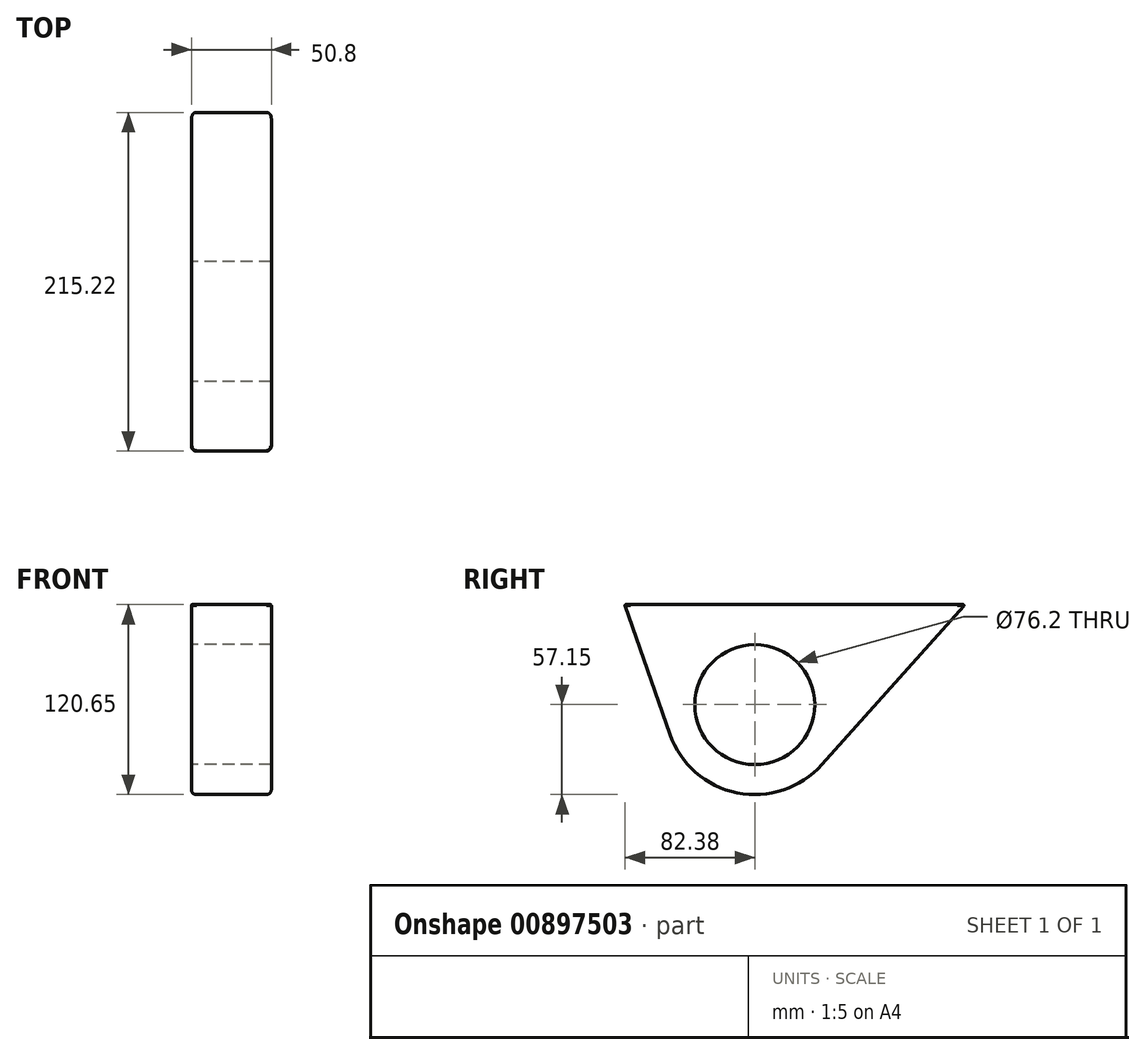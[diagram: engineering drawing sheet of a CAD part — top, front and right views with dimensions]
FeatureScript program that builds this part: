
annotation { "Feature Type Name" : "Feature", "Feature Type Description" : "" }
export const myFeature = defineFeature(function(context is Context, id is Id, definition is map)
    precondition{}
    {
        {
            var Q0;
            Q0=qCreatedBy(makeId("Right.planeOp"),FACE);
            var sketch = newSketch(context, id + "F0", { "sketchPlane" : qUnion([Q0])});
            skCircle(sketch, "E0", {"center": v(0, 0) * mm, "radius": 38.1 * mm});
            skCircle(sketch, "E1.0", {"center": v(0, 0) * mm, "radius": 57.15 * mm});
            skLineSegment(sketch, "E2", {"start": v(-82.55, 63.5) * mm, "end": v(133.35, 63.5) * mm});
            skLineSegment(sketch, "E3", {"start": v(0, 0) * mm, "end": v(0, 63.5) * mm, "construction": true});
            skLineSegment(sketch, "E4", {"start": v(-82.55, 63.5) * mm, "end": v(-53.99, -18.75) * mm});
            skLineSegment(sketch, "E5", {"start": v(133.35, 63.5) * mm, "end": v(42.62, -38.07) * mm});
            skSolve(sketch);
        }
        {
            var Q0;
            Q0=makeQuery(id+"F0.imprint","IMPRINT",FACE,{"disambiguationData":[TD([[makeQuery(id+"F0.imprint","IMPRINT",EDGE,{"derivedFrom":sQuery(id+"F0.wireOp",EDGE,"E0")}),-1.0]])]});
            var Q1;
            Q1=makeQuery(id+"F0.imprint","IMPRINT",FACE,{"disambiguationData":[TD([[makeQuery(id+"F0.imprint","IMPRINT",EDGE,{"derivedFrom":sQuery(id+"F0.wireOp",EDGE,"E2")}),-1.0]])]});
            extrude(context, id + "F1", {"entities" : qUnion([Q0, Q1]), "depth" : 50.8 * mm, "offsetDistance" : 25.4 * mm});
        }
        {
            var Q0;
            Q0=makeQuery(id+"F1.opExtrude","CAP_EDGE",EDGE,{"disambiguationData":[OSD([sQuery(id+"F0.wireOp",EDGE,"E0")])],"isStart":true});
            var Q1;
            Q1=makeQuery(id+"F1.opExtrude","CAP_EDGE",EDGE,{"disambiguationData":[OSD([sQuery(id+"F0.wireOp",EDGE,"E0")])],"isStart":false});
            var Q2;
            Q2=makeQuery(id+"F1.opExtrude","CAP_EDGE",EDGE,{"disambiguationData":[OSD([sQuery(id+"F0.wireOp",EDGE,"E2")])],"isStart":false});
            var Q3;
            Q3=makeQuery(id+"F1.opExtrude","SWEPT_EDGE",EDGE,{"disambiguationData":[OSD([sQuery(id+"F0.wireOp",EDGE,"E2"),sQuery(id+"F0.wireOp",EDGE,"E5")])]});
            var Q4;
            Q4=makeQuery(id+"F1.opExtrude","CAP_EDGE",EDGE,{"disambiguationData":[OSD([sQuery(id+"F0.wireOp",EDGE,"E2")])],"isStart":true});
            var Q5;
            Q5=makeQuery(id+"F1.opExtrude","SWEPT_EDGE",EDGE,{"disambiguationData":[OSD([sQuery(id+"F0.wireOp",EDGE,"E2"),sQuery(id+"F0.wireOp",EDGE,"E4")])]});
            fillet(context, id + "F2", {"entities" : qUnion([Q0, Q1, Q2, Q3, Q4, Q5]), "radius" : 0.4 * mm, "tangentPropagation" : true, "allowEdgeOverflow" : false});
        }
        {
            var Q0;
            Q0=makeQuery(id+"F1.opExtrude","CAP_EDGE",EDGE,{"disambiguationData":[OSD([sQuery(id+"F0.wireOp",EDGE,"E4")])],"isStart":false});
            var Q1;
            Q1=makeQuery(id+"F1.opExtrude","CAP_EDGE",EDGE,{"disambiguationData":[OSD([sQuery(id+"F0.wireOp",EDGE,"E4")])],"isStart":true});
            fillet(context, id + "F3", {"entities" : qUnion([Q0, Q1]), "radius" : 3.17 * mm, "tangentPropagation" : true, "allowEdgeOverflow" : false});
        }
    });
